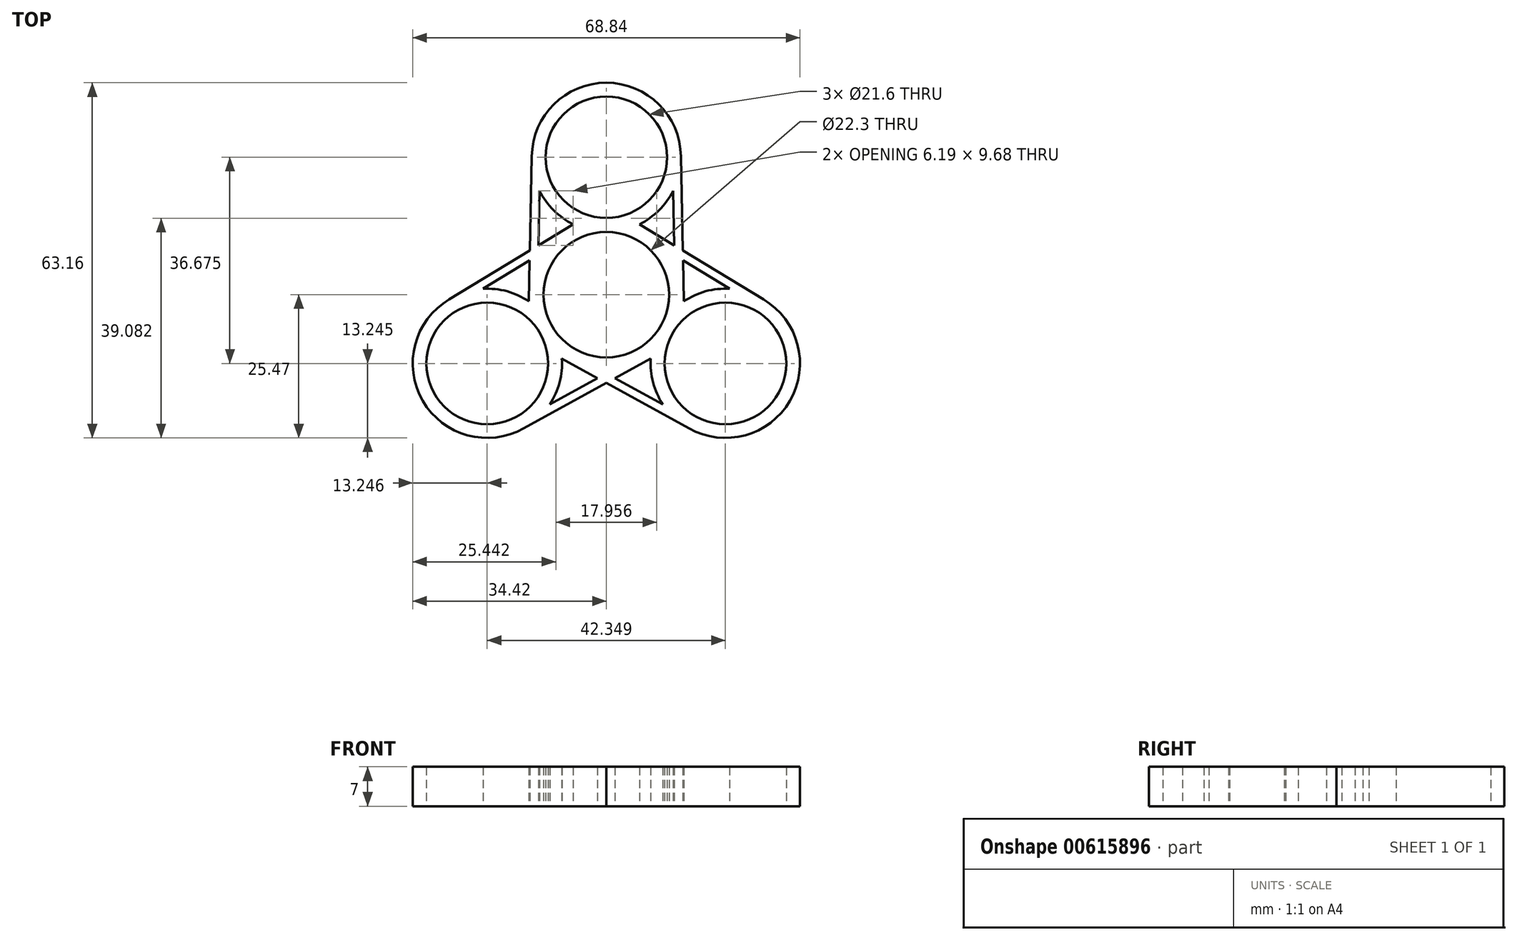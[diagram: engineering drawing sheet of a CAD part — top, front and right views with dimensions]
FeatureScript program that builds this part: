
annotation { "Feature Type Name" : "Feature", "Feature Type Description" : "" }
export const myFeature = defineFeature(function(context is Context, id is Id, definition is map)
    precondition{}
    {
        {
            var Q0;
            Q0=qCreatedBy(makeId("Top.planeOp"),FACE);
            var sketch = newSketch(context, id + "F0", { "sketchPlane" : qUnion([Q0])});
            skCircle(sketch, "E0", {"center": v(0, 0) * mm, "radius": 11.15 * mm});
            skLineSegment(sketch, "E1", {"start": v(0, 0) * mm, "end": v(0, 24.45) * mm});
            skCircle(sketch, "E2", {"center": v(0, 24.45) * mm, "radius": 10.8 * mm});
            skCircle(sketch, "E3.1.0", {"center": v(-21.17, -12.22) * mm, "radius": 10.8 * mm});
            skCircle(sketch, "E3.2.0", {"center": v(21.17, -12.22) * mm, "radius": 10.8 * mm});
            skLineSegment(sketch, "E4", {"start": v(13.24, 24.6) * mm, "end": v(21.15, 26.19) * mm});
            skLineSegment(sketch, "E5", {"start": v(13.24, 24.6) * mm, "end": v(13.6, 7.85) * mm});
            skLineSegment(sketch, "E6.0", {"start": v(11.87, 18.45) * mm, "end": v(12.08, 8.77) * mm});
            skLineSegment(sketch, "E7.1.0", {"start": v(-27.92, -0.83) * mm, "end": v(-13.6, 7.85) * mm});
            skLineSegment(sketch, "E7.1.1", {"start": v(-21.92, 1.05) * mm, "end": v(-13.63, 6.07) * mm});
            skLineSegment(sketch, "E7.2.0", {"start": v(14.68, -23.77) * mm, "end": v(0, -15.7) * mm});
            skLineSegment(sketch, "E7.2.1", {"start": v(10.05, -19.5) * mm, "end": v(1.56, -14.84) * mm});
            skLineSegment(sketch, "E8.MirrorCS", {"start": v(-11.87, 18.45) * mm, "end": v(-12.08, 8.77) * mm});
            skLineSegment(sketch, "E9.MirrorCS", {"start": v(-13.24, 24.6) * mm, "end": v(-13.6, 7.85) * mm});
            skLineSegment(sketch, "E10.1.0", {"start": v(-10.05, -19.5) * mm, "end": v(-1.56, -14.84) * mm});
            skLineSegment(sketch, "E10.1.1", {"start": v(-14.68, -23.77) * mm, "end": v(0, -15.7) * mm});
            skLineSegment(sketch, "E10.2.0", {"start": v(21.92, 1.05) * mm, "end": v(13.63, 6.07) * mm});
            skLineSegment(sketch, "E10.2.1", {"start": v(27.92, -0.83) * mm, "end": v(13.6, 7.85) * mm});
            skLineSegment(sketch, "E11.trimOffspring", {"start": v(12.08, 8.77) * mm, "end": v(5.88, 12.52) * mm});
            skLineSegment(sketch, "E12.trimOffspring", {"start": v(13.63, 6.07) * mm, "end": v(13.78, -1.17) * mm});
            skArc(sketch, "E13", {"start": v(21.92, 1.05) * mm, "mid": v(17.67, 0.6) * mm, "end": v(13.78, -1.17) * mm});
            skArc(sketch, "E14", {"start": v(11.87, 18.45) * mm, "mid": v(9.36, 15) * mm, "end": v(5.88, 12.52) * mm});
            skArc(sketch, "E15", {"start": v(-5.88, 12.52) * mm, "mid": v(-9.36, 15) * mm, "end": v(-11.87, 18.45) * mm});
            skArc(sketch, "E16", {"start": v(13.24, 24.6) * mm, "mid": v(0, 37.7) * mm, "end": v(-13.24, 24.6) * mm});
            skArc(sketch, "E17", {"start": v(-13.78, -1.17) * mm, "mid": v(-17.67, 0.6) * mm, "end": v(-21.92, 1.05) * mm});
            skArc(sketch, "E18", {"start": v(-27.92, -0.83) * mm, "mid": v(-32.64, -18.85) * mm, "end": v(-14.68, -23.77) * mm});
            skArc(sketch, "E19", {"start": v(-7.9, -11.35) * mm, "mid": v(-8.31, -15.6) * mm, "end": v(-10.05, -19.5) * mm});
            skArc(sketch, "E20", {"start": v(7.9, -11.35) * mm, "mid": v(8.31, -15.6) * mm, "end": v(10.05, -19.5) * mm});
            skArc(sketch, "E21", {"start": v(27.92, -0.83) * mm, "mid": v(32.64, -18.85) * mm, "end": v(14.68, -23.77) * mm});
            skLineSegment(sketch, "E22.trimOffspring", {"start": v(-12.08, 8.77) * mm, "end": v(-5.88, 12.52) * mm});
            skLineSegment(sketch, "E23.trimOffspring", {"start": v(-13.63, 6.07) * mm, "end": v(-13.78, -1.17) * mm});
            skLineSegment(sketch, "E24.trimOffspring", {"start": v(-1.56, -14.84) * mm, "end": v(-7.9, -11.35) * mm});
            skLineSegment(sketch, "E25.trimOffspring", {"start": v(1.56, -14.84) * mm, "end": v(7.9, -11.35) * mm});
            skSolve(sketch);
        }
        {
            var Q0;
            Q0 = qSketchRegion(id + "F0", true);
            extrude(context, id + "F1", {"entities" : qUnion([Q0]), "depth" : 7 * mm, "offsetDistance" : 25 * mm});
        }
    });
